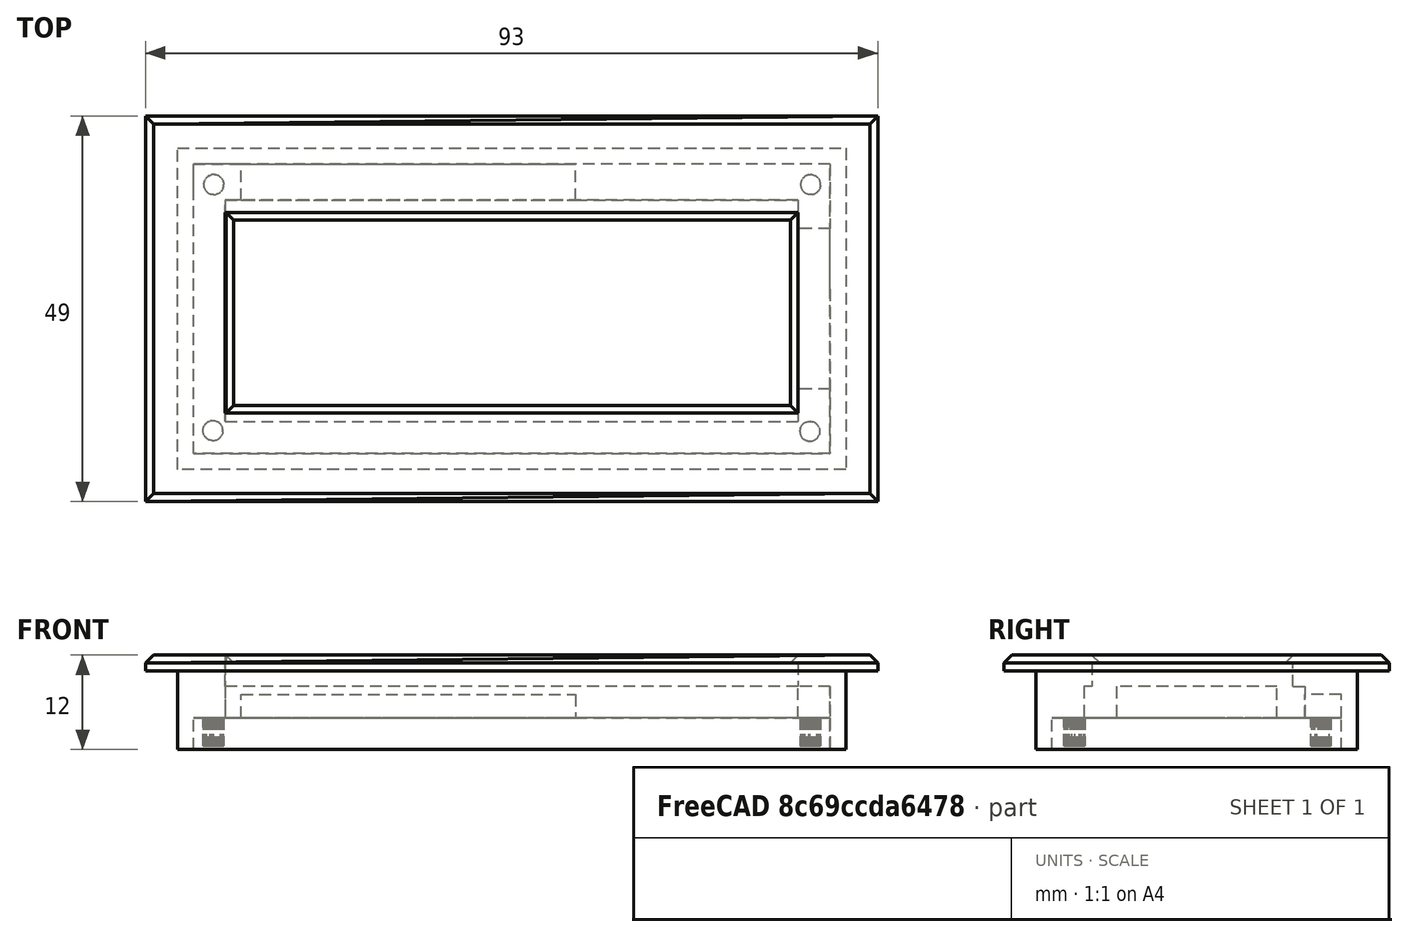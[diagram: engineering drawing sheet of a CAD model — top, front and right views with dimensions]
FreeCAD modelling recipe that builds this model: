
FCSTD DOCUMENT  (FreeCAD 1.0R39109 (Git))
Label: alarm_top_box
License: All rights reserved
LicenseURL: http://en.wikipedia.org/wiki/All_rights_reserved
objects: Part::Box×15, TechDraw::DrawViewDimension×10, Part::Cut×5, TechDraw::DrawProjGroupItem×3, Part::Feature×2, Part::MultiFuse×2, TechDraw::DrawSVGTemplate×2, TechDraw::DrawPage×2, Mesh::Feature×1, Part::Refine×1, TechDraw::DrawProjGroup×1, TechDraw::FeatureProjection×1, TechDraw::DrawViewImage×1
note: 46 computed .brp shape members not serialized (recipe doc carries the construction recipe); baked Part::Feature solids carry a one-line shape summary decoded from their .brp

FEATURE [Part::Box] Box007  label="front001"
  AttacherType = Attacher::AttachEngine3D
  Height = 4
  Length = 167
  Width = 70
FEATURE [Part::Box] Box003  label="left"
  AttacherType = Attacher::AttachEngine3D
  Height = 40
  Length = 4
  Placement = pos=(0,0,-40) rot=(0,0,1;0rad)
  Width = 70
FEATURE [Part::Box] Box005  label="top_wall"
  AttacherType = Attacher::AttachEngine3D
  Height = 40
  Length = 167
  Placement = pos=(0,66,-40) rot=(0,0,1;0rad)
  Width = 4
FEATURE [Part::Box] Box004  label="right"
  AttacherType = Attacher::AttachEngine3D
  Height = 40
  Length = 4
  Placement = pos=(163,0,-40) rot=(0,0,1;0rad)
  Width = 70
FEATURE [Part::Box] Box002  label="bottom"
  AttacherType = Attacher::AttachEngine3D
  Height = 15
  Length = 167
  Placement = pos=(0,0,-15) rot=(0,0,1;0rad)
  Width = 4
FEATURE [Mesh::Feature] _602_LCD_Bezel  label="1602_LCD_Bezel"
  Placement = pos=(109.3,47.2,4.1) rot=(0,1,0;3.14159rad)
FEATURE [Part::Feature] _602_LCD_Bezel001
  shape: bbox 93 x 49 x 12 mm, 1212 faces, 0 solids (baked)
FEATURE [Part::Feature] _602_LCD_Bezel001_solid  label="_602_LCD_Bezel001 (Solid)"
  shape: bbox 93 x 49 x 12 mm, 1212 faces (baked)
FEATURE [Part::Refine] _602_LCD_Bezel001_solid001  label="_602_LCD_Bezel001 (Solid)001"
  Placement = pos=(171.6,88.9,0) rot=(0,0,1;3.14159rad)
  Source = -> _602_LCD_Bezel001_solid
FEATURE [Part::Box] Box  label="cut out"
  AttacherType = Attacher::AttachEngine3D
  Height = 4
  Length = 80
  Placement = pos=(47,25,0) rot=(0,0,1;0rad)
  Width = 40
FEATURE [Part::Cut] Cut  label="Breakout for LCD"
  Base = -> Box007
  Tool = -> Box
FEATURE [Part::MultiFuse] Fusion  label="Front with display"
  Shapes = -> [Cut,_602_LCD_Bezel001_solid001]
FEATURE [Part::Box] Box008  label="Quader"
  AttacherType = Attacher::AttachEngine3D
  Height = 10
  Length = 5
  Placement = pos=(155,11,-10) rot=(0,0,1;0rad)
  Width = 1.75
FEATURE [Part::Box] Box009  label="Quader001"
  AttacherType = Attacher::AttachEngine3D
  Height = 10
  Length = 8
  Placement = pos=(155,9,-10) rot=(0,0,1;0rad)
  Width = 5.75
FEATURE [Part::Cut] Cut001  label="left_pcb"
  Base = -> Box009
  Tool = -> Box008
FEATURE [Part::Box] Box010  label="Quader002"
  AttacherType = Attacher::AttachEngine3D
  Height = 10
  Length = 8
  Placement = pos=(85.7,9,-10) rot=(0,0,1;0rad)
  Width = 5.75
FEATURE [Part::Box] Box011  label="Quader003"
  AttacherType = Attacher::AttachEngine3D
  Height = 10
  Length = 5
  Placement = pos=(88.7,11,-10) rot=(0,0,1;0rad)
  Width = 1.75
FEATURE [Part::Cut] Cut002  label="right_pcb"
  Base = -> Box010
  Placement = pos=(5,0,0) rot=(0,0,1;0rad)
  Tool = -> Box011
FEATURE [Part::Box] Box012  label="Quader004"
  AttacherType = Attacher::AttachEngine3D
  Height = 10
  Length = 8
  Placement = pos=(85.7,9,-10) rot=(0,0,1;0rad)
  Width = 5.75
FEATURE [Part::Box] Box013  label="Quader005"
  AttacherType = Attacher::AttachEngine3D
  Height = 10
  Length = 5
  Placement = pos=(88.7,11,-10) rot=(0,0,1;0rad)
  Width = 1.5
FEATURE [Part::Cut] Cut003  label="right_power"
  Base = -> Box012
  Placement = pos=(-81.7,0,0) rot=(0,0,1;0rad)
  Tool = -> Box013
FEATURE [Part::Box] Box014  label="Quader006"
  AttacherType = Attacher::AttachEngine3D
  Height = 10
  Length = 5
  Placement = pos=(155,11,-10) rot=(0,0,1;0rad)
  Width = 1.5
FEATURE [Part::Box] Box015  label="Quader007"
  AttacherType = Attacher::AttachEngine3D
  Height = 10
  Length = 8
  Placement = pos=(155,9,-10) rot=(0,0,1;0rad)
  Width = 5.75
FEATURE [Part::Cut] Cut004  label="left_pcb001"
  Base = -> Box015
  Placement = pos=(-89,0,0) rot=(0,0,1;0rad)
  Tool = -> Box014
FEATURE [Part::Box] Box017  label="Quader009"
  AttacherType = Attacher::AttachEngine3D
  Height = 10
  Length = 16.7
  Placement = pos=(74,9,-10) rot=(0,0,1;0rad)
  Width = 5.7
FEATURE [Part::MultiFuse] Fusion001
  Shapes = -> [Box003,Box005,Box004,Box002,Fusion,Cut001,Cut002,Cut003,Cut004,Box017]
FEATURE [TechDraw::DrawProjGroupItem] ProjItem002  label="Untersicht"
  CoarseView = false
  Direction = (1e-16,0,1)
  Focus = 100
  HardHidden = false
  IsoCount = 0
  IsoHidden = false
  IsoVisible = false
  LockPosition = false
  Perspective = false
  Rotation = 0
  RotationVector = (1,0,0)
  Scale = 0.75
  ScaleType = 0
  ScrubCount = 1
  SeamHidden = false
  SeamVisible = false
  SmoothHidden = false
  SmoothVisible = true
  Source = -> [Fusion001]
  Type = 5
  X = 0
  XDirection = (-1,0,1e-16)
  Y = 57.7875
FEATURE [TechDraw::DrawSVGTemplate] Template001  label="Vorlage001"
  Height = 210
  Orientation = 1
  Template = /Applications/FreeCAD.app/Contents/Resources/share/Mod/TechDraw/Templates/A4_Landscape_TD.svg
  Width = 297
FEATURE [TechDraw::DrawProjGroupItem] View001  label="Front001"
  CoarseView = false
  Direction = (0,-1,0)
  Focus = 100
  HardHidden = false
  IsoCount = 0
  IsoHidden = false
  IsoVisible = false
  LockPosition = true
  Perspective = false
  Rotation = 0
  RotationVector = (1,0,0)
  ScaleType = 2
  ScrubCount = 1
  SeamHidden = false
  SeamVisible = false
  SmoothHidden = false
  SmoothVisible = true
  Source = -> [Fusion001]
  Type = 0
  X = 0
  XDirection = (1,0,0)
  Y = 0
FEATURE [TechDraw::DrawProjGroupItem] ProjItem003  label="View inside"
  CoarseView = false
  Direction = (0,0,-1)
  Focus = 100
  HardHidden = false
  IsoCount = 0
  IsoHidden = false
  IsoVisible = false
  LockPosition = false
  Perspective = false
  Rotation = 0
  RotationVector = (1,0,0)
  ScaleType = 0
  ScrubCount = 1
  SeamHidden = false
  SeamVisible = false
  SmoothHidden = false
  SmoothVisible = true
  Source = -> [Fusion001]
  Type = 5
  X = 0
  XDirection = (1,0,0)
  Y = 33.8586
FEATURE [TechDraw::DrawProjGroup] ProjGroup001
  Anchor = -> View001
  AutoDistribute = true
  LockPosition = false
  ProjectionType = 0
  Rotation = 0
  ScaleType = 0
  Source = -> [Fusion001]
  Views = -> [View001,ProjItem003]
  X = 148.5
  Y = 105
  spacingX = 15
  spacingY = 15
FEATURE [TechDraw::DrawViewDimension] Dimension002  label="Maß002"
  AngleOverride = false
  Arbitrary = false
  ArbitraryTolerances = false
  BoxCorners = (2) [(-83.5,-35,0),(83.5,35,0)]
  EqualTolerance = true
  ExtensionAngle = 0
  FormatSpec = %.2w
  FormatSpecOverTolerance = %+.2w
  FormatSpecUnderTolerance = %+.2w
  Inverted = false
  LineAngle = 0
  LockPosition = false
  MeasureType = 1
  OverTolerance = 0
  References2D = -> [ProjItem003]
  Rotation = 0
  ScaleType = 0
  TheoreticalExact = false
  Type = 1
  UnderTolerance = 0
  X = 0
  Y = -52.9408
FEATURE [TechDraw::DrawViewDimension] Dimension003  label="Maß003"
  AngleOverride = false
  Arbitrary = false
  ArbitraryTolerances = false
  BoxCorners = (2) [(-83.5,-35,0),(83.5,35,0)]
  EqualTolerance = true
  ExtensionAngle = 0
  FormatSpec = %.2w
  FormatSpecOverTolerance = %+.2w
  FormatSpecUnderTolerance = %+.2w
  Inverted = false
  LineAngle = 0
  LockPosition = false
  MeasureType = 1
  OverTolerance = 0
  References2D = -> [ProjItem003]
  Rotation = 0
  ScaleType = 0
  TheoreticalExact = false
  Type = 2
  UnderTolerance = 0
  X = -93.1272
  Y = 28.5
FEATURE [TechDraw::DrawViewDimension] Dimension004  label="Maß004"
  AngleOverride = false
  Arbitrary = false
  ArbitraryTolerances = false
  BoxCorners = (2) [(-83.5,-35,0),(83.5,35,0)]
  EqualTolerance = true
  ExtensionAngle = 0
  FormatSpec = %.2w
  FormatSpecOverTolerance = %+.2w
  FormatSpecUnderTolerance = %+.2w
  Inverted = false
  LineAngle = 0
  LockPosition = false
  MeasureType = 1
  OverTolerance = 0
  References2D = -> [ProjItem003]
  Rotation = 0
  ScaleType = 0
  TheoreticalExact = false
  Type = 2
  UnderTolerance = 0
  X = -63.9928
  Y = 23.25
FEATURE [TechDraw::DrawViewDimension] Dimension005  label="Maß005"
  AngleOverride = false
  Arbitrary = false
  ArbitraryTolerances = false
  BoxCorners = (2) [(-83.5,-35,0),(83.5,35,0)]
  EqualTolerance = true
  ExtensionAngle = 0
  FormatSpec = %.2w
  FormatSpecOverTolerance = %+.2w
  FormatSpecUnderTolerance = %+.2w
  Inverted = false
  LineAngle = 0
  LockPosition = false
  MeasureType = 1
  OverTolerance = 0
  References2D = -> [ProjItem003]
  Rotation = 0
  ScaleType = 0
  TheoreticalExact = false
  Type = 2
  UnderTolerance = 0
  X = 23.2371
  Y = 23.125
FEATURE [TechDraw::DrawViewDimension] Dimension006  label="Maß006"
  AngleOverride = false
  Arbitrary = false
  ArbitraryTolerances = false
  BoxCorners = (2) [(-83.5,-35,0),(83.5,35,0)]
  EqualTolerance = true
  ExtensionAngle = 0
  FormatSpec = %.2w
  FormatSpecOverTolerance = %+.2w
  FormatSpecUnderTolerance = %+.2w
  Inverted = false
  LineAngle = 0
  LockPosition = false
  MeasureType = 1
  OverTolerance = 0
  References2D = -> [ProjItem003]
  Rotation = 0
  ScaleType = 0
  TheoreticalExact = false
  Type = 1
  UnderTolerance = 0
  X = 0
  Y = -63.7289
FEATURE [TechDraw::DrawViewDimension] Dimension007  label="Maß007"
  AngleOverride = false
  Arbitrary = false
  ArbitraryTolerances = false
  BoxCorners = (2) [(-83.5,-35,0),(83.5,35,0)]
  EqualTolerance = true
  ExtensionAngle = 0
  FormatSpec = %.2w
  FormatSpecOverTolerance = %+.2w
  FormatSpecUnderTolerance = %+.2w
  Inverted = false
  LineAngle = 0
  LockPosition = false
  MeasureType = 1
  OverTolerance = 0
  References2D = -> [ProjItem003]
  Rotation = 0
  ScaleType = 0
  TheoreticalExact = false
  Type = 1
  UnderTolerance = 0
  X = -75.5
  Y = 10.6843
FEATURE [TechDraw::DrawViewDimension] Dimension008  label="Maß008"
  AngleOverride = false
  Arbitrary = false
  ArbitraryTolerances = false
  BoxCorners = (2) [(-83.5,-35,0),(83.5,35,0)]
  EqualTolerance = true
  ExtensionAngle = 0
  FormatSpec = %.2w
  FormatSpecOverTolerance = %+.2w
  FormatSpecUnderTolerance = %+.2w
  Inverted = false
  LineAngle = 0
  LockPosition = false
  MeasureType = 1
  OverTolerance = 0
  References2D = -> [ProjItem003]
  Rotation = 0
  ScaleType = 0
  TheoreticalExact = false
  Type = 1
  UnderTolerance = 0
  X = 75.5
  Y = 12.1038
FEATURE [TechDraw::DrawViewDimension] Dimension013  label="Maß013"
  AngleOverride = false
  Arbitrary = false
  ArbitraryTolerances = false
  BoxCorners = (2) [(-83.5,-35,0),(83.5,35,0)]
  EqualTolerance = true
  ExtensionAngle = 0
  FormatSpec = %.2w
  FormatSpecOverTolerance = %+.2w
  FormatSpecUnderTolerance = %+.2w
  Inverted = false
  LineAngle = 0
  LockPosition = false
  MeasureType = 1
  OverTolerance = 0
  References2D = -> [ProjItem003]
  Rotation = 0
  ScaleType = 0
  TheoreticalExact = false
  Type = 1
  UnderTolerance = 0
  X = -44.5
  Y = 21.2013
FEATURE [TechDraw::DrawViewDimension] Dimension  label="Maß"
  AngleOverride = false
  Arbitrary = false
  ArbitraryTolerances = false
  BoxCorners = (2) [(-83.5,-35,0),(83.5,35,0)]
  EqualTolerance = true
  ExtensionAngle = 0
  FormatSpec = %.2w
  FormatSpecOverTolerance = %+.2w
  FormatSpecUnderTolerance = %+.2w
  Inverted = false
  LineAngle = 0
  LockPosition = false
  MeasureType = 1
  OverTolerance = 0
  References2D = -> [ProjItem003]
  Rotation = 0
  ScaleType = 0
  TheoreticalExact = false
  Type = 1
  UnderTolerance = 0
  X = -77.5
  Y = 42.3962
FEATURE [TechDraw::DrawViewDimension] Dimension014  label="Maß014"
  AngleOverride = false
  Arbitrary = false
  ArbitraryTolerances = false
  BoxCorners = (2) [(-83.5,-35,0),(83.5,35,0)]
  EqualTolerance = true
  ExtensionAngle = 0
  FormatSpec = %.2w
  FormatSpecOverTolerance = %+.2w
  FormatSpecUnderTolerance = %+.2w
  Inverted = false
  LineAngle = 0
  LockPosition = false
  MeasureType = 1
  OverTolerance = 0
  References2D = -> [ProjItem003]
  Rotation = 0
  ScaleType = 0
  TheoreticalExact = false
  Type = 1
  UnderTolerance = 0
  X = 43.35
  Y = 42.3962
FEATURE [TechDraw::DrawPage] Page001  label="Seite001"
  KeepUpdated = true
  NextBalloonIndex = 1
  ProjectionType = 0
  Template = -> Template001
  Views = -> [ProjGroup001,Dimension002,Dimension003,Dimension004,Dimension005,Dimension006,Dimension007,Dimension008,Dimension013,Dimension,Dimension014]
FEATURE [TechDraw::DrawSVGTemplate] Template002  label="Vorlage002"
  EditableTexts = approval_person=Thomas Lüth; creator=TLC IT Consulting; date_of_issue=30.04.25; document_type=3D Drawing; general_tolerances=ISO 2768-m; identification_number=2; language_code=EN; part_material=PLA+; revision_index=AAA; sheet_number=2 / 2; sheet_scale=1 : 1; title=alarm_top_box
  Height = 210
  Orientation = 1
  Template = /Applications/FreeCAD.app/Contents/Resources/share/Mod/TechDraw/Templates/A4_Landscape_ISO5457_minimal.svg
  Width = 297
FEATURE [TechDraw::FeatureProjection] Fusion001_proj
  Direction = (-0.012339,0.035719,-0.999286)
  HCompound = false
  IsoLineHCompound = false
  IsoLineVCompound = true
  OutLineHCompound = false
  OutLineVCompound = true
  Rg1LineHCompound = false
  Rg1LineVCompound = true
  RgNLineHCompound = false
  RgNLineVCompound = true
  Source = -> Fusion001
  VCompound = true
FEATURE [TechDraw::DrawViewImage] ActiveView  label="3D View inside"
  Height = 102.4
  ImageFile = <userpath>/Library/Caches/FreeCAD/Cache/FreeCAD_Doc_f0394a2b-91e8-439e-b46d-526a44a1e718_878403_122209/Page002ActiveViewkodeEI.png
  LockPosition = false
  Rotation = 0
  ScaleType = 2
  Width = 128
  X = 162.988
  Y = 134.272
FEATURE [TechDraw::DrawPage] Page002  label="Seite002"
  KeepUpdated = true
  NextBalloonIndex = 1
  ProjectionType = 0
  Template = -> Template002
  Views = -> [ActiveView]
